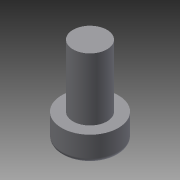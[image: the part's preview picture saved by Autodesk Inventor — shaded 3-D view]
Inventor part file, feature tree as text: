
AUTODESK INVENTOR PART (.ipt)
format: ipt  version: 2015 (Build 190159000, 159)  size: 94,208 bytes
history: native  units: mm
features: extrude x2, sketch x2, fillet x1
ambient origin geometry x8: Origin, YZ Plane, XZ Plane, XY Plane, X Axis, Y Axis, Z Axis, Center Point
bodies: Solid1 (feature_tree)
feature tree (5):
  extrude  "Extrusion1"  Depth=7.7mm TaperAngle=0.0deg
  extrude  "Extrusion2"  Depth=5.5mm TaperAngle=0.0deg
  fillet  "Fillet1"  Radius=0.4mm
  sketch  "Sketch1"  dims[d0=5.0mm d1=7.7mm d2=0.0mm]
  sketch  "Sketch2"  dims[d3=3.0mm d4=5.5mm d5=0.0mm d6=0.4mm]
